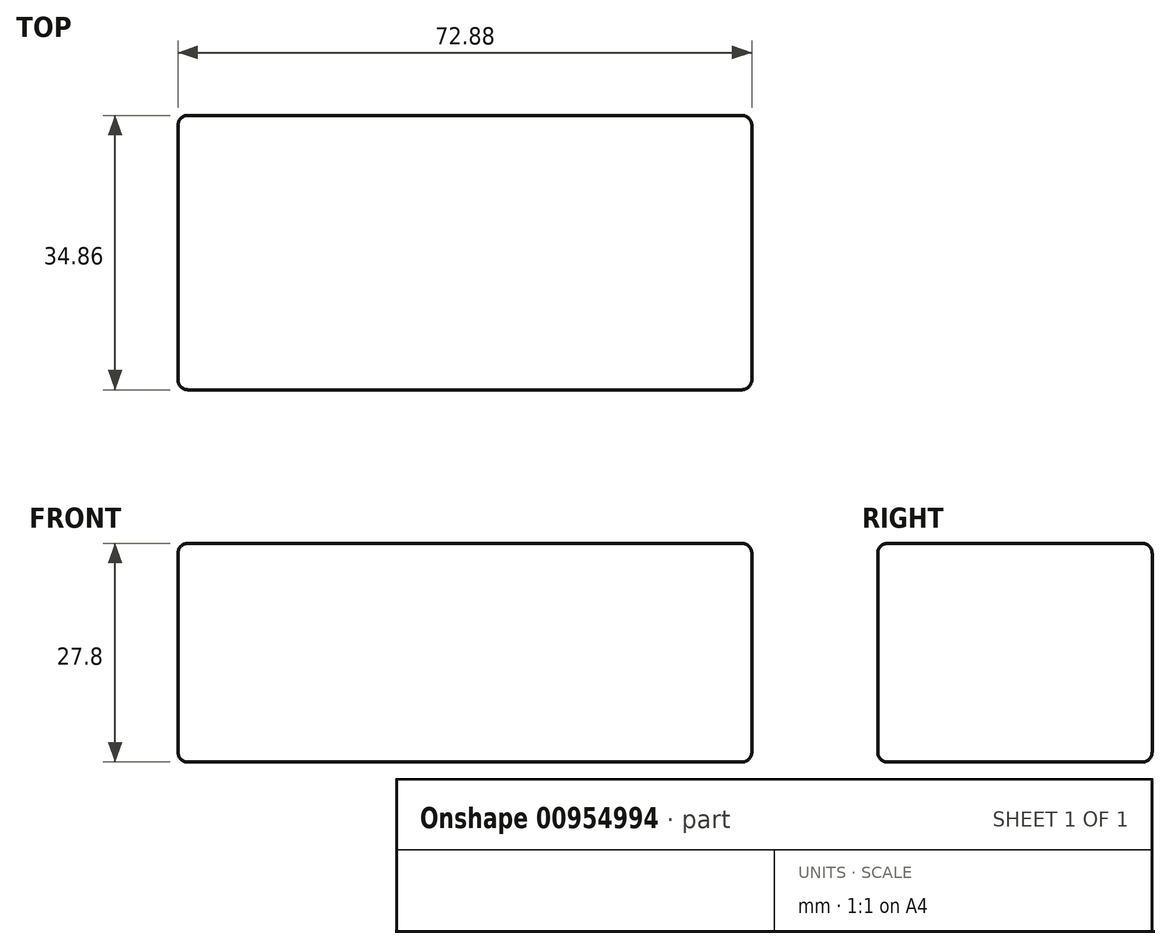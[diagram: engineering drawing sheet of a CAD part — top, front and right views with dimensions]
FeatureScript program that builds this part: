
annotation { "Feature Type Name" : "Feature", "Feature Type Description" : "" }
export const myFeature = defineFeature(function(context is Context, id is Id, definition is map)
    precondition{}
    {
        {
            var Q0;
            Q0=qCreatedBy(makeId("Top.planeOp"),FACE);
            var sketch = newSketch(context, id + "F0", { "sketchPlane" : qUnion([Q0])});
            skLineSegment(sketch, "E0.bottom", {"start": v(36.44, 17.43) * mm, "end": v(-36.44, 17.43) * mm});
            skLineSegment(sketch, "E0.top", {"start": v(36.44, -17.43) * mm, "end": v(-36.44, -17.43) * mm});
            skLineSegment(sketch, "E0.left", {"start": v(36.44, 17.43) * mm, "end": v(36.44, -17.43) * mm});
            skLineSegment(sketch, "E0.right", {"start": v(-36.44, 17.43) * mm, "end": v(-36.44, -17.43) * mm});
            skPoint(sketch, "E0.middle", {"position": v(0, 0) * mm});
            skSolve(sketch);
        }
        {
            var Q0;
            Q0 = qSketchRegion(id + "F0", true);
            extrude(context, id + "F1", {"entities" : qUnion([Q0]), "depth" : 27.8 * mm, "offsetDistance" : 25.4 * mm});
        }
        {
            var Q0;
            Q0=makeQuery(id+"F1.opExtrude","CAP_FACE",FACE,{"disambiguationData":[OSD([sQuery(id+"F0.wireOp",EDGE,"E0.bottom"),sQuery(id+"F0.wireOp",EDGE,"E0.top"),sQuery(id+"F0.wireOp",EDGE,"E0.left"),sQuery(id+"F0.wireOp",EDGE,"E0.right")])],"isStart":false});
            var Q1;
            Q1=makeQuery(id+"F1.opExtrude","SWEPT_FACE",FACE,{"disambiguationData":[OSD([sQuery(id+"F0.wireOp",EDGE,"E0.top")])]});
            var Q2;
            Q2=makeQuery(id+"F1.opExtrude","SWEPT_FACE",FACE,{"disambiguationData":[OSD([sQuery(id+"F0.wireOp",EDGE,"E0.left")])]});
            var Q3;
            Q3=makeQuery(id+"F1.opExtrude","CAP_FACE",FACE,{"disambiguationData":[OSD([sQuery(id+"F0.wireOp",EDGE,"E0.bottom"),sQuery(id+"F0.wireOp",EDGE,"E0.top"),sQuery(id+"F0.wireOp",EDGE,"E0.left"),sQuery(id+"F0.wireOp",EDGE,"E0.right")])],"isStart":true});
            var Q4;
            Q4=makeQuery(id+"F1.opExtrude","SWEPT_FACE",FACE,{"disambiguationData":[OSD([sQuery(id+"F0.wireOp",EDGE,"E0.bottom")])]});
            fillet(context, id + "F2", {"entities" : qUnion([Q0, Q1, Q2, Q3, Q4]), "radius" : 1.27 * mm, "tangentPropagation" : true, "allowEdgeOverflow" : false});
        }
    });
